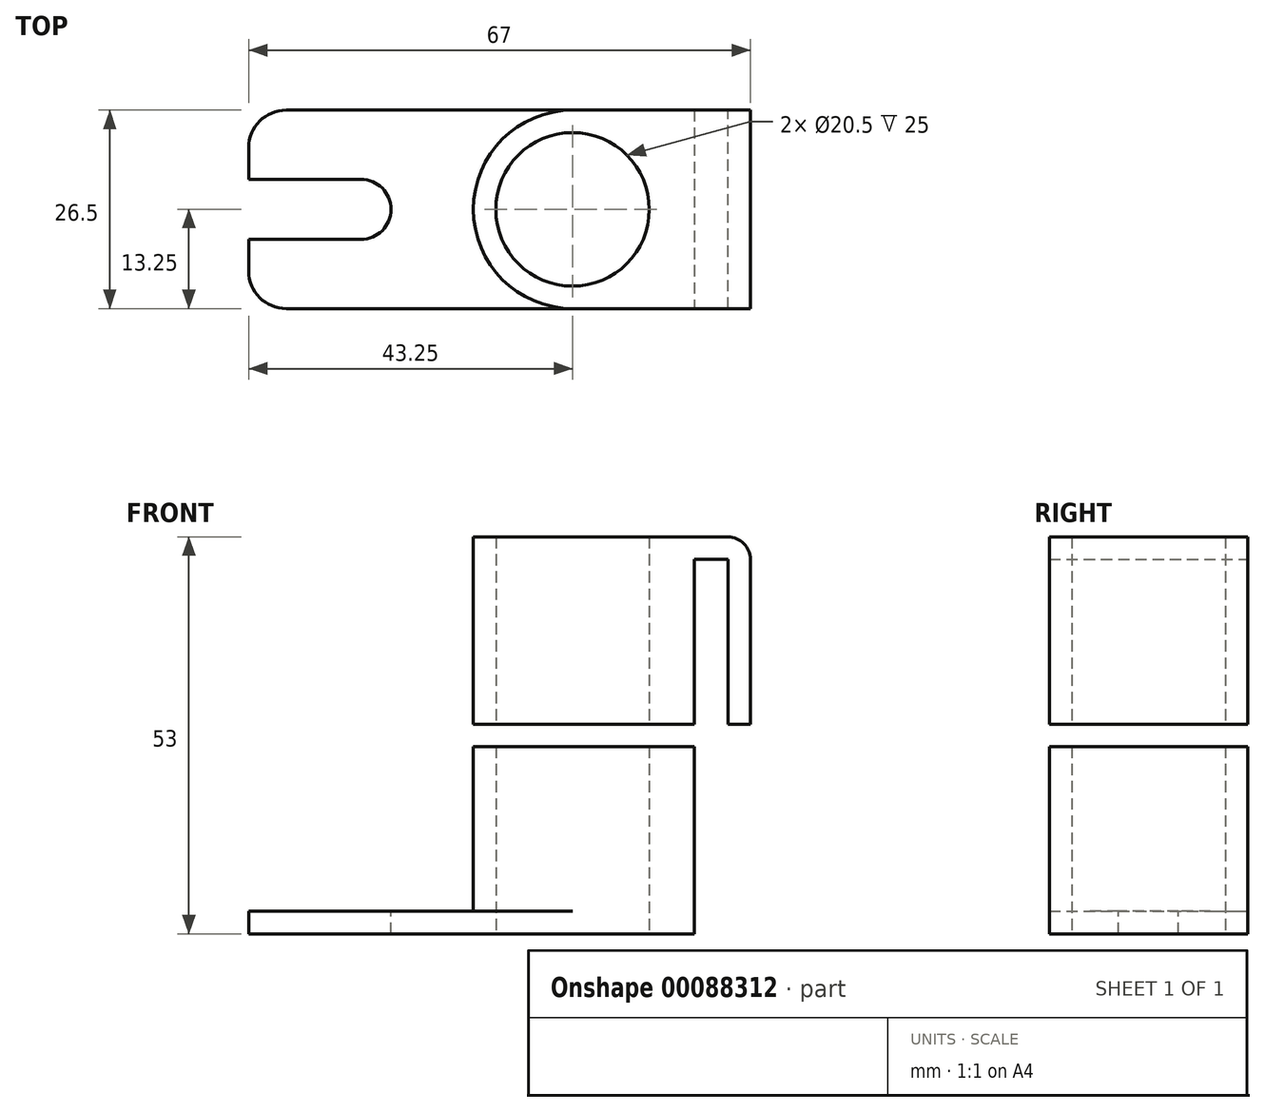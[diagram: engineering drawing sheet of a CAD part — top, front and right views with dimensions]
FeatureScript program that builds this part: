
annotation { "Feature Type Name" : "Feature", "Feature Type Description" : "" }
export const myFeature = defineFeature(function(context is Context, id is Id, definition is map)
    precondition{}
    {
        {
            var Q0;
            Q0=qCreatedBy(makeId("Top.planeOp"),FACE);
            var sketch = newSketch(context, id + "F0", { "sketchPlane" : qUnion([Q0])});
            skCircle(sketch, "E0", {"center": v(0, 0) * mm, "radius": 10.25 * mm});
            skCircle(sketch, "E1", {"center": v(0, 0) * mm, "radius": 13.25 * mm});
            skLineSegment(sketch, "E2", {"start": v(0, 13.25) * mm, "end": v(23.75, 13.25) * mm});
            skLineSegment(sketch, "E3", {"start": v(23.75, 13.25) * mm, "end": v(23.75, -13.25) * mm});
            skLineSegment(sketch, "E4", {"start": v(0, -13.25) * mm, "end": v(23.75, -13.25) * mm});
            skLineSegment(sketch, "E5", {"start": v(13.25, 0) * mm, "end": v(13.25, 13.25) * mm});
            skLineSegment(sketch, "E6", {"start": v(13.25, 0) * mm, "end": v(13.25, -13.25) * mm});
            skLineSegment(sketch, "E7", {"start": v(16.25, 13.25) * mm, "end": v(16.25, -13.25) * mm, "construction": true});
            skLineSegment(sketch, "E8", {"start": v(20.75, 13.25) * mm, "end": v(20.75, -13.25) * mm, "construction": true});
            skLineSegment(sketch, "E9", {"start": v(16.25, 13.25) * mm, "end": v(16.25, -13.25) * mm});
            skLineSegment(sketch, "E10", {"start": v(20.75, -13.25) * mm, "end": v(20.75, 13.25) * mm});
            skSolve(sketch);
        }
        {
            var Q0;
            Q0=qSketchRegion(id+"F0",true);
            extrude(context, id + "F1", {"entities" : qUnion([Q0]), "depth" : 3 * mm});
        }
        {
            var Q0;
            Q0=makeQuery(id+"F0.imprint","IMPRINT",FACE,{"disambiguationData":[TD([[makeQuery(id+"F0.imprint","IMPRINT",EDGE,{"derivedFrom":sQuery(id+"F0.wireOp",EDGE,"E0")}),-1.0]])]});
            var Q1;
            {var subQ3=sQuery(id+"F0.wireOp",EDGE,"E5");Q1=makeQuery(id+"F0.imprint","IMPRINT",FACE,{"disambiguationData":[TD([[makeQuery(id+"F0.imprint","IMPRINT",EDGE,{"derivedFrom":subQ3}),1.0]])]});}
            var Q2;
            {var subQ1=sQuery(id+"F0.wireOp",EDGE,"E5");Q2=makeQuery(id+"F0.imprint","IMPRINT",FACE,{"disambiguationData":[TD([[makeQuery(id+"F0.imprint","IMPRINT",EDGE,{"derivedFrom":subQ1}),-1.0]])]});}
            var Q3;
            {var subQ0=sQuery(id+"F0.wireOp",EDGE,"E3");Q3=makeQuery(id+"F0.imprint","IMPRINT",FACE,{"disambiguationData":[TD([[makeQuery(id+"F0.imprint","IMPRINT",EDGE,{"derivedFrom":subQ0}),-1.0]])]});}
            var Q4;
            {var subQ3=sQuery(id+"F0.wireOp",EDGE,"E6");Q4=makeQuery(id+"F0.imprint","IMPRINT",FACE,{"disambiguationData":[TD([[makeQuery(id+"F0.imprint","IMPRINT",EDGE,{"derivedFrom":subQ3}),-1.0]])]});}
            extrude(context, id + "F2", {"entities" : qUnion([Q0, Q1, Q2, Q3, Q4]), "operationType" : NewBodyOperationType.ADD, "oppositeDirection" : true, "depth" : 22 * mm});
        }
        {
            var Q0;
            Q0=makeQuery(id+"F2.opExtrude","CAP_EDGE",EDGE,{"disambiguationData":[OSD([sQuery(id+"F0.wireOp",EDGE,"E9")])],"isStart":true});
            var Q1;
            Q1=makeQuery(id+"F2.opExtrude","CAP_EDGE",EDGE,{"disambiguationData":[OSD([sQuery(id+"F0.wireOp",EDGE,"E10")])],"isStart":true});
            var Q2;
            Q2=makeQuery(id+"F1.opExtrude","CAP_EDGE",EDGE,{"disambiguationData":[OSD([sQuery(id+"F0.wireOp",EDGE,"E3")])],"isStart":false});
            fillet(context, id + "F3", {"entities" : qUnion([Q0, Q1, Q2]), "radius" : 3 * mm, "tangentPropagation" : true, "allowEdgeOverflow" : false});
        }
        {
            var Q0;
            Q0=makeQuery(id+"F2.opExtrude","CAP_FACE",FACE,{"disambiguationData":[OSD([sQuery(id+"F0.wireOp",EDGE,"E0"),sQuery(id+"F0.wireOp",EDGE,"E1"),sQuery(id+"F0.wireOp",EDGE,"E2"),sQuery(id+"F0.wireOp",EDGE,"E4"),sQuery(id+"F0.wireOp",EDGE,"E9")])],"isStart":false});
            cPlane(context, id + "F4", {"entities" : qUnion([Q0]), "cplaneType" : CPlaneType.OFFSET, "offset" : 25 * mm, "width" : 150 * mm, "height" : 150 * mm});
        }
        {
            var Q0;
            Q0=qCreatedBy(id+"F4.planeOp",FACE);
            var sketch = newSketch(context, id + "F5", { "sketchPlane" : qUnion([Q0])});
            skCircle(sketch, "E11.0", {"center": v(0, 0) * mm, "radius": 10.25 * mm});
            skArc(sketch, "E12.0.0", {"start": v(0, 13.25) * mm, "mid": v(-13.25, 0) * mm, "end": v(0, -13.25) * mm});
            skLineSegment(sketch, "E12.0.1", {"start": v(0, -13.25) * mm, "end": v(16.25, -13.25) * mm});
            skLineSegment(sketch, "E12.0.2", {"start": v(16.25, -13.25) * mm, "end": v(16.25, 13.25) * mm});
            skLineSegment(sketch, "E12.0.3", {"start": v(16.25, 13.25) * mm, "end": v(0, 13.25) * mm});
            skLineSegment(sketch, "E13", {"start": v(0, -13.25) * mm, "end": v(-43.25, -13.25) * mm});
            skLineSegment(sketch, "E14", {"start": v(-43.25, -13.25) * mm, "end": v(-43.25, -4) * mm});
            skLineSegment(sketch, "E15", {"start": v(-43.25, 13.25) * mm, "end": v(0, 13.25) * mm});
            skLineSegment(sketch, "E16.bottom", {"start": v(0, 0) * mm, "end": v(-28.25, 0) * mm, "construction": true});
            skLineSegment(sketch, "E16.top", {"start": v(0, 4) * mm, "end": v(-43.25, 4) * mm, "construction": true});
            skLineSegment(sketch, "E16.left", {"start": v(0, 0) * mm, "end": v(0, 4) * mm, "construction": true});
            skLineSegment(sketch, "E17.MirrorCS", {"start": v(0, -4) * mm, "end": v(-43.25, -4) * mm, "construction": true});
            skLineSegment(sketch, "E18", {"start": v(-43.25, 0) * mm, "end": v(-13.25, 0) * mm, "construction": true});
            skPoint(sketch, "E19", {"position": v(-28.25, 0) * mm});
            skArc(sketch, "E20", {"start": v(-28.25, -4) * mm, "mid": v(-24.25, 0) * mm, "end": v(-28.25, 4) * mm});
            skLineSegment(sketch, "E21", {"start": v(-28.25, 4) * mm, "end": v(-43.25, 4) * mm});
            skLineSegment(sketch, "E22", {"start": v(-43.25, -4) * mm, "end": v(-28.25, -4) * mm});
            skLineSegment(sketch, "E23.trimOffspring", {"start": v(-43.25, 4) * mm, "end": v(-43.25, 13.25) * mm});
            skSolve(sketch);
        }
        {
            var Q0;
            Q0=makeQuery(id+"F5.imprint","IMPRINT",FACE,{"disambiguationData":[TD([[makeQuery(id+"F5.imprint","IMPRINT",EDGE,{"derivedFrom":sQuery(id+"F5.wireOp",EDGE,"E11.0")}),-1.0]])]});
            extrude(context, id + "F6", {"entities" : qUnion([Q0]), "oppositeDirection" : true, "depth" : 22 * mm});
        }
        {
            var Q0;
            Q0=qSketchRegion(id+"F5",true);
            extrude(context, id + "F7", {"entities" : qUnion([Q0]), "operationType" : NewBodyOperationType.ADD, "depth" : 3 * mm});
        }
        {
            var Q0;
            Q0=makeQuery(id+"F7.opExtrude","SWEPT_EDGE",EDGE,{"disambiguationData":[OSD([sQuery(id+"F5.wireOp",EDGE,"E15"),sQuery(id+"F5.wireOp",EDGE,"E23.trimOffspring")])]});
            var Q1;
            Q1=makeQuery(id+"F7.opExtrude","SWEPT_EDGE",EDGE,{"disambiguationData":[OSD([sQuery(id+"F5.wireOp",EDGE,"E13"),sQuery(id+"F5.wireOp",EDGE,"E14")])]});
            fillet(context, id + "F8", {"entities" : qUnion([Q0, Q1]), "radius" : 5 * mm, "tangentPropagation" : true, "allowEdgeOverflow" : false});
        }
    });
